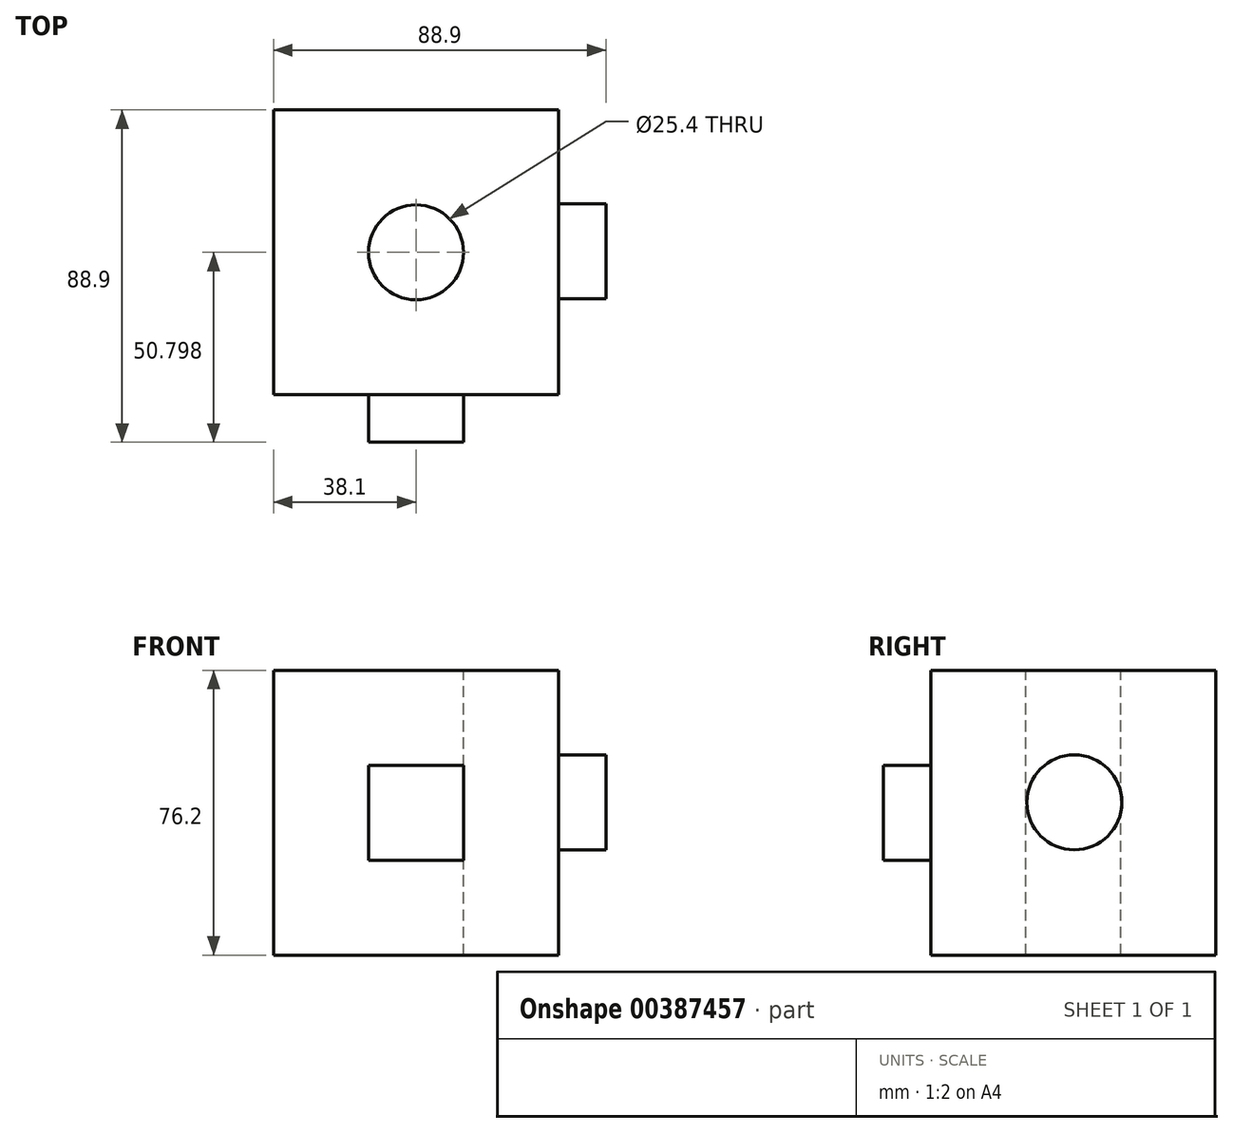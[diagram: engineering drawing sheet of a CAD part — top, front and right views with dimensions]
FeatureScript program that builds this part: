
annotation { "Feature Type Name" : "Feature", "Feature Type Description" : "" }
export const myFeature = defineFeature(function(context is Context, id is Id, definition is map)
    precondition{}
    {
        {
            var Q0;
            Q0=qCreatedBy(makeId("Top.planeOp"),FACE);
            var sketch = newSketch(context, id + "F0", { "sketchPlane" : qUnion([Q0])});
            skLineSegment(sketch, "E0.bottom", {"start": v(0, 65) * mm, "end": v(76.2, 65) * mm});
            skLineSegment(sketch, "E0.top", {"start": v(0, -11.2) * mm, "end": v(76.2, -11.2) * mm});
            skLineSegment(sketch, "E0.left", {"start": v(0, 65) * mm, "end": v(0, -11.2) * mm});
            skLineSegment(sketch, "E0.right", {"start": v(76.2, 65) * mm, "end": v(76.2, -11.2) * mm});
            skSolve(sketch);
        }
        {
            var Q0;
            Q0=makeQuery(id+"F0.imprint","IMPRINT",FACE,{"disambiguationData":[TD([[makeQuery(id+"F0.imprint","IMPRINT",EDGE,{"derivedFrom":sQuery(id+"F0.wireOp",EDGE,"E0.bottom")}),-1.0]])]});
            extrude(context, id + "F1", {"entities" : qUnion([Q0]), "depth" : 76.2 * mm});
        }
        {
            var Q0;
            Q0=makeQuery(id+"F1.opExtrude","CAP_FACE",FACE,{"disambiguationData":[OSD([sQuery(id+"F0.wireOp",EDGE,"E0.bottom"),sQuery(id+"F0.wireOp",EDGE,"E0.top"),sQuery(id+"F0.wireOp",EDGE,"E0.left"),sQuery(id+"F0.wireOp",EDGE,"E0.right")])],"isStart":false});
            var sketch = newSketch(context, id + "F2", { "sketchPlane" : qUnion([Q0])});
            skPoint(sketch, "E1", {"position": v(0, 65) * mm});
            skPoint(sketch, "E2", {"position": v(38.1, 26.9) * mm});
            skPoint(sketch, "E2.positionSnap0", {"position": v(0, 26.9) * mm});
            skPoint(sketch, "E2.positionSnap1", {"position": v(38.1, 65) * mm});
            skSolve(sketch);
        }
        {
            var Q0;
            Q0=sQuery(id+"F2.wireOp",VERTEX,"E2");
            var Q1;
            Q1=makeQuery(id+"F1.opExtrude","SWEPT_BODY",BODY,{"disambiguationData":[OSD([sQuery(id+"F0.wireOp",EDGE,"E0.bottom"),sQuery(id+"F0.wireOp",EDGE,"E0.top"),sQuery(id+"F0.wireOp",EDGE,"E0.left"),sQuery(id+"F0.wireOp",EDGE,"E0.right")])]});
            hole(context, id + "F3", {"style" : HoleStyle.SIMPLE, "endStyle" : HoleEndStyle.THROUGH, "holeDiameter" : 25.4 * mm, "isTappedThrough" : true, "tappedDepth" : 12.7 * mm, "tapClearance" : 3, "locations" : qUnion([Q0]), "scope" : qUnion([Q1])});
        }
        {
            var Q0;
            Q0=makeQuery(id+"F1.opExtrude","SWEPT_FACE",FACE,{"disambiguationData":[OSD([sQuery(id+"F0.wireOp",EDGE,"E0.top")])]});
            var sketch = newSketch(context, id + "F4", { "sketchPlane" : qUnion([Q0])});
            skLineSegment(sketch, "E3.bottom", {"start": v(25.4, 50.8) * mm, "end": v(50.8, 50.8) * mm});
            skLineSegment(sketch, "E3.top", {"start": v(25.4, 25.4) * mm, "end": v(50.8, 25.4) * mm});
            skLineSegment(sketch, "E3.left", {"start": v(25.4, 50.8) * mm, "end": v(25.4, 25.4) * mm});
            skLineSegment(sketch, "E3.right", {"start": v(50.8, 50.8) * mm, "end": v(50.8, 25.4) * mm});
            skSolve(sketch);
        }
        {
            var Q0;
            Q0=makeQuery(id+"F4.imprint","IMPRINT",FACE,{"disambiguationData":[TD([[makeQuery(id+"F4.imprint","IMPRINT",EDGE,{"derivedFrom":sQuery(id+"F4.wireOp",EDGE,"E3.bottom")}),-1.0]])]});
            extrude(context, id + "F5", {"entities" : qUnion([Q0]), "operationType" : NewBodyOperationType.ADD, "depth" : 12.7 * mm});
        }
        {
            var Q0;
            Q0=makeQuery(id+"F1.opExtrude","SWEPT_FACE",FACE,{"disambiguationData":[OSD([sQuery(id+"F0.wireOp",EDGE,"E0.right")])]});
            var sketch = newSketch(context, id + "F6", { "sketchPlane" : qUnion([Q0])});
            skCircle(sketch, "E4", {"center": v(27.18, 40.86) * mm, "radius": 12.7 * mm});
            skSolve(sketch);
        }
        {
            var Q0;
            Q0=makeQuery(id+"F6.imprint","IMPRINT",FACE,{"disambiguationData":[TD([[makeQuery(id+"F6.imprint","IMPRINT",EDGE,{"derivedFrom":sQuery(id+"F6.wireOp",EDGE,"E4")}),1.0]])]});
            extrude(context, id + "F7", {"entities" : qUnion([Q0]), "operationType" : NewBodyOperationType.ADD, "depth" : 12.7 * mm});
        }
    });
